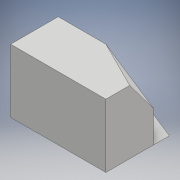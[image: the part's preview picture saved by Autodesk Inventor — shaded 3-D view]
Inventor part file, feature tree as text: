
AUTODESK INVENTOR PART (.ipt)
format: ipt  version: 2018 (Build 220112000, 112)  size: 150,016 bytes
history: native  units: mm
features: extrude x6, sketch x5, chamfer x2, other x2, loft x1
ambient origin geometry x8: Origin, YZ Plane, XZ Plane, XY Plane, X Axis, Y Axis, Z Axis, Center Point
bodies: Body1 (feature_tree)
feature tree (16):
  sketch  "Sketch3"  dims[d6=20.0mm d7=20.0mm d8=15.0mm d9=0.0mm]
  extrude  "Extrusion2"  Depth=20.0mm
  chamfer  "Chamfer3"  Distance=15.0mm
  extrude  "Extrusion3"  Depth=5.0mm TaperAngle=45.0deg
  extrude  "Extrusion5"  Depth=5.0mm TaperAngle=45.0deg
  chamfer  "Chamfer4"  Distance=12.0mm
  sketch  "Sketch7"  dims[d28=5.0mm d29=0.0mm d30=8.32mm d31=5.0mm d32=45.0deg]
  extrude  "Extrusion6"  TaperAngle=90.0deg  [1 undecoded]
  extrude  "Extrusion7"  Depth=10.0mm TaperAngle=0.0deg
  loft  "Loft1"
  extrude  "Extrusion10"  TaperAngle=0.0deg  [1 undecoded]
  sketch  "Sketch6"  dims[d13=15.0mm d14=0.0mm d21=5.0mm d22=10.0mm d23=45.0deg]
  sketch  "Sketch8"  dims[d33=7.5mm]
  other  "Edges1"
  other  "Edges2"
  sketch  "Sketch14"  dims[d35=180.0deg d36=12.0mm d37=90.0deg d38=10.0mm d39=0.0mm d40=10.0mm d41=0.0mm d46=0.0mm d47=90.0deg d48=0.0mm d49=90.0deg d53=5.0mm d54=0.0mm]
note: 2 required parameter values undecoded (feature->parameter linkage not recoverable at this tier; creation-order binding heuristic only, values carry confidence <= 0.55)
